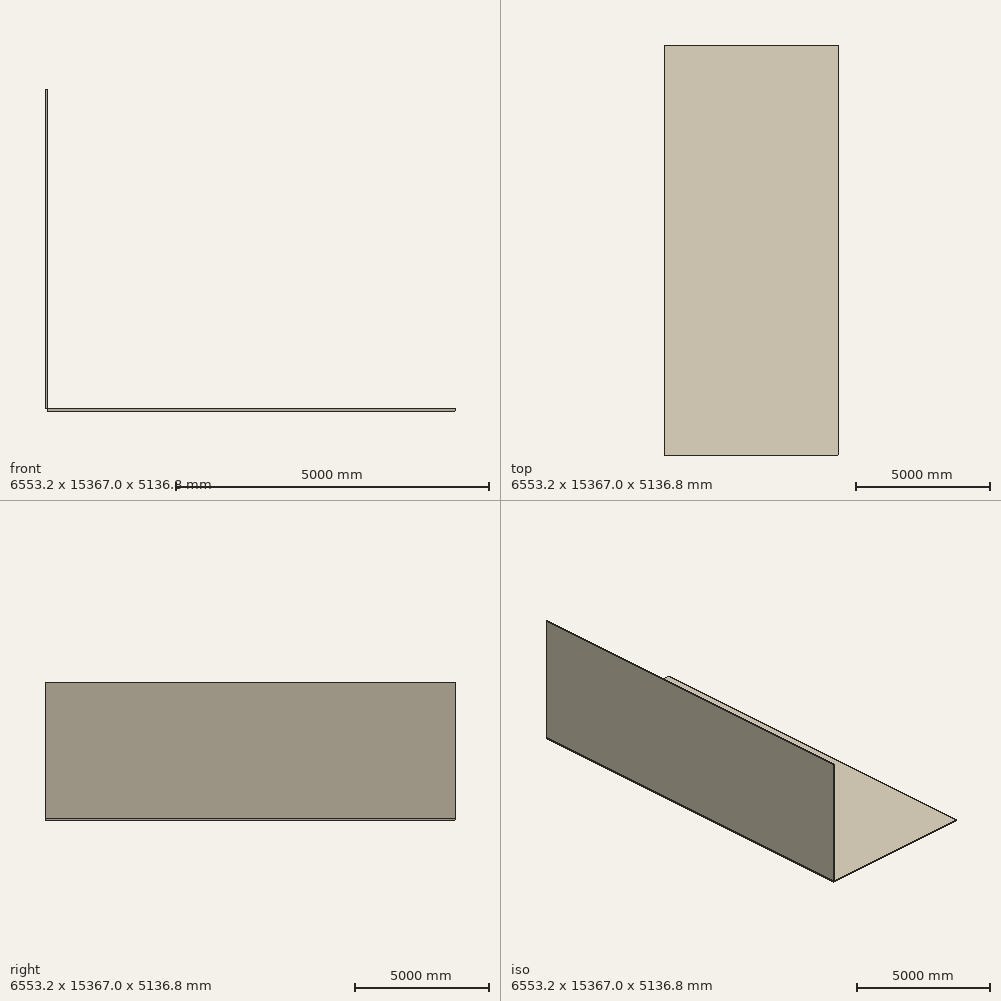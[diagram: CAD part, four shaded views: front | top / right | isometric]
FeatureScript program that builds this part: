
annotation { "Feature Type Name" : "Feature", "Feature Type Description" : "" }
export const myFeature = defineFeature(function(context is Context, id is Id, definition is map)
    precondition{}
    {
        {
            var Q0;
            Q0=qCreatedBy(makeId("Top.planeOp"),FACE);
            var sketch = newSketch(context, id + "F0", { "sketchPlane" : qUnion([Q0])});
            skLineSegment(sketch, "E0.bottom", {"start": v(-269.8, 15058.4) * mm, "end": v(6258, 15058.4) * mm});
            skLineSegment(sketch, "E0.top", {"start": v(-269.8, -308.6) * mm, "end": v(6258, -308.6) * mm});
            skLineSegment(sketch, "E0.left", {"start": v(-269.8, 15058.4) * mm, "end": v(-269.8, -308.6) * mm});
            skLineSegment(sketch, "E0.right", {"start": v(6258, 15058.4) * mm, "end": v(6258, -308.6) * mm});
            skSolve(sketch);
        }
        {
            var Q0;
            Q0=makeQuery(id+"F0.imprint","IMPRINT",FACE,{"disambiguationData":[TD([[makeQuery(id+"F0.imprint","IMPRINT",EDGE,{"derivedFrom":sQuery(id+"F0.wireOp",EDGE,"E0.bottom")}),-1.0]])]});
            extrude(context, id + "F1", {"entities" : qUnion([Q0]), "endBound" : BoundingType.SYMMETRIC, "depth" : 50.8 * mm, "offsetDistance" : 25.4 * mm});
        }
        {
            var Q0;
            Q0=makeQuery(id+"F1.opExtrude","SWEPT_FACE",FACE,{"disambiguationData":[OSD([sQuery(id+"F0.wireOp",EDGE,"E0.left")])]});
            var sketch = newSketch(context, id + "F2", { "sketchPlane" : qUnion([Q0])});
            skLineSegment(sketch, "E1.bottom", {"start": v(308.6, 25.4) * mm, "end": v(-15058.4, 25.4) * mm});
            skLineSegment(sketch, "E1.top", {"start": v(308.6, 5111.4) * mm, "end": v(-15058.4, 5111.4) * mm});
            skLineSegment(sketch, "E1.left", {"start": v(308.6, 25.4) * mm, "end": v(308.6, 5111.4) * mm});
            skLineSegment(sketch, "E1.right", {"start": v(-15058.4, 25.4) * mm, "end": v(-15058.4, 5111.4) * mm});
            skSolve(sketch);
        }
        {
            var Q0;
            Q0=makeQuery(id+"F2.imprint","IMPRINT",FACE,{"disambiguationData":[TD([[makeQuery(id+"F2.imprint","IMPRINT",EDGE,{"derivedFrom":sQuery(id+"F2.wireOp",EDGE,"E1.top")}),1.0]])]});
            extrude(context, id + "F3", {"entities" : qUnion([Q0]), "depth" : 25.4 * mm, "offsetDistance" : 25.4 * mm});
        }
    });
